# Revit family: Eelectron_Inwall_AD84A02KNX
name_source: partatom
category: Electrical Equipment
revit_build: Autodesk Revit 2016 (Build: 20161004_0715(x64)
units: mm (PartAtom-declared; Revit-internal decimal feet)

## family parameters
Cut with Voids When Loaded = No
Host = Face
Part Type = Other Panel
Room Calculation Point = No
Round Connector Dimension = Use Diameter
Shared = No

## types (1)
- IO32D01KNX
    Analog Input for Infrared Receiver (IRX) = These accessories must be used:
IR01A01ACC (IRX with cable and connector)
RC80A01IRC (Telecomando 8 canali)
    Analog Input for temperature probe = For NTC temperature probe eelectron code
TS01A01ACC (range from -20°C to +100°C)
TS01B01ACC (range from -50°C to +60°C)
Max. length of Connecting Cable: ≤ 20 m (twisted cable)
    Bus = SELV DC 21..31 V DC
    CE Mark = Yes
    Case = Plastic (Nylon)
    Date of publishing = 13/03/2018
    Default Elevation = 1219.2 mm  [stored 4 ft]
    Degree of pollution EN 60664-1 = 2
    Degree of protection EN 60529 = IP20
    Description = INWALL 3 IN / 2 OUT MODULE
    Diameter = 52 mm
    Digital input = For free potential contacts (dry contacts)
Max. length of Connecting Cable: ≤ 30 m (twisted cable)
Voltage Scanning: 3,3 V DC (internally Generated)
AWG24 cables with 180 mm length
    Edition number = rev. 0.0
    Height = 28 mm  [stored 0.0918635 ft]
    Manufacturer = Eelectron S.p.a.
    Max Ambient temperature = 45 °C
    Max Storage temperature = 55 °C
    Min Ambient temperature = -551 °C
    Min Storage temperature = 20 °C
    Model = IO32D01KNX
    Others = Meets EN 50491-3
    Overvoltage class IEC664-1 = III
    Relative humidity Max = 90%
    Safety Class IEC 1140 = III
    URL = http://www.eelectron.com
    Weight = 0.05 kg

note: [stored X ft] marks values corroborated as IEEE doubles in the binary element streams (Revit-internal decimal feet)
